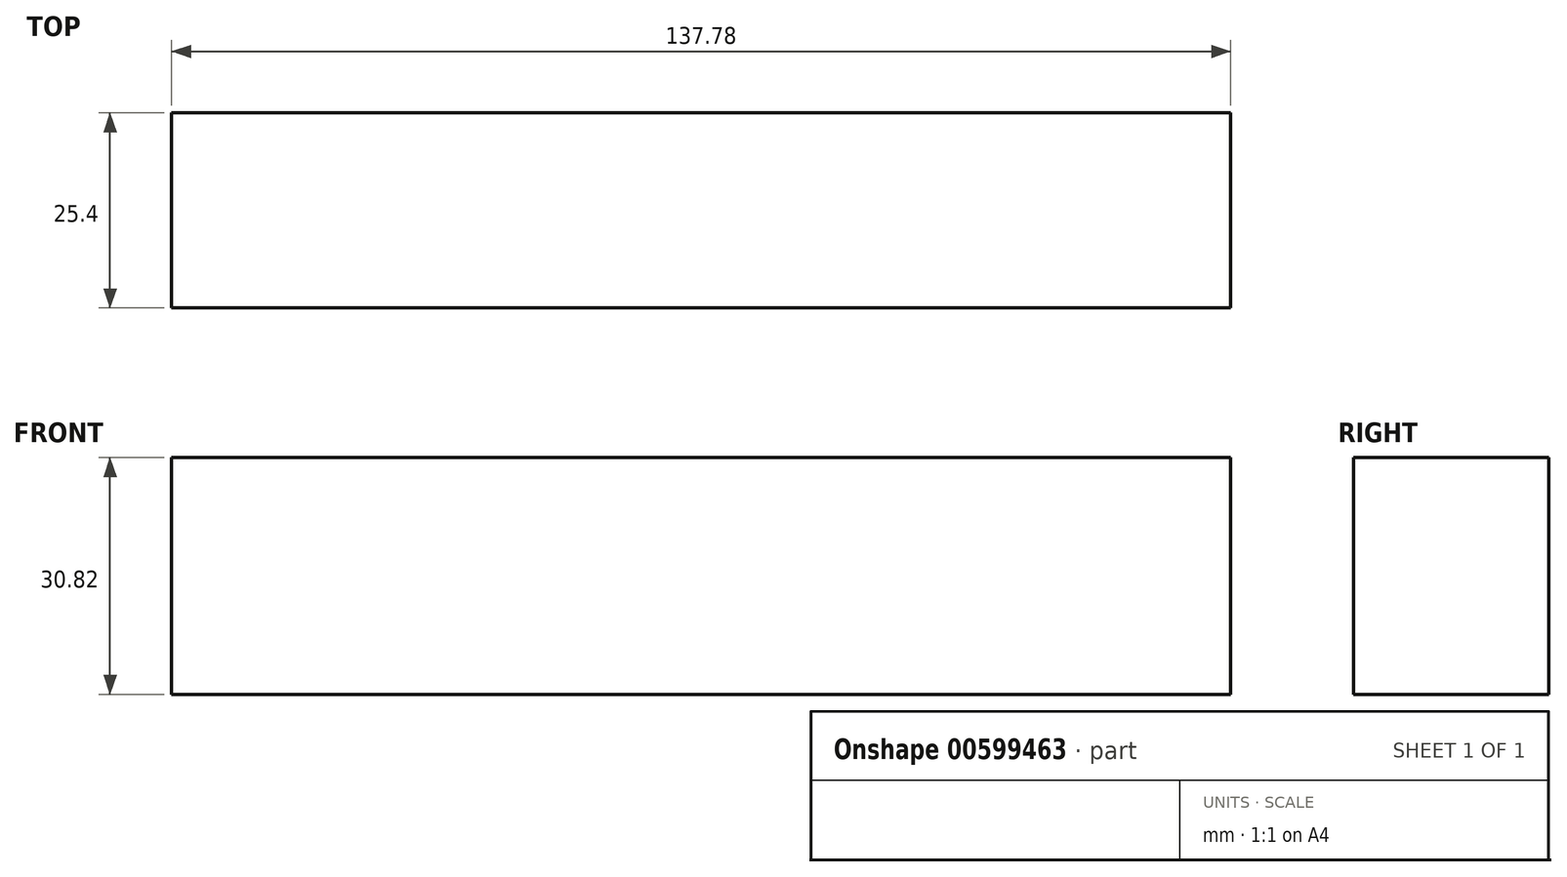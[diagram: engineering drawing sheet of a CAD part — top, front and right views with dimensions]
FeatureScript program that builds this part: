
annotation { "Feature Type Name" : "Feature", "Feature Type Description" : "" }
export const myFeature = defineFeature(function(context is Context, id is Id, definition is map)
    precondition{}
    {
        {
            var Q0;
            Q0=qCreatedBy(makeId("Front.planeOp"),FACE);
            var sketch = newSketch(context, id + "F0", { "sketchPlane" : qUnion([Q0])});
            skLineSegment(sketch, "E0.bottom", {"start": v(68.89, 15.41) * mm, "end": v(-68.89, 15.41) * mm});
            skLineSegment(sketch, "E0.top", {"start": v(68.89, -15.41) * mm, "end": v(-68.89, -15.41) * mm});
            skLineSegment(sketch, "E0.left", {"start": v(68.89, 15.41) * mm, "end": v(68.89, -15.41) * mm});
            skLineSegment(sketch, "E0.right", {"start": v(-68.89, 15.41) * mm, "end": v(-68.89, -15.41) * mm});
            skPoint(sketch, "E0.middle", {"position": v(0, 0) * mm});
            skSolve(sketch);
        }
        {
            var Q0;
            Q0=makeQuery(id+"F0.imprint","IMPRINT",FACE,{"disambiguationData":[TD([[makeQuery(id+"F0.imprint","IMPRINT",EDGE,{"derivedFrom":sQuery(id+"F0.wireOp",EDGE,"E0.bottom")}),1.0]])]});
            extrude(context, id + "F1", {"entities" : qUnion([Q0]), "depth" : 25.4 * mm, "offsetDistance" : 25.4 * mm});
        }
    });
